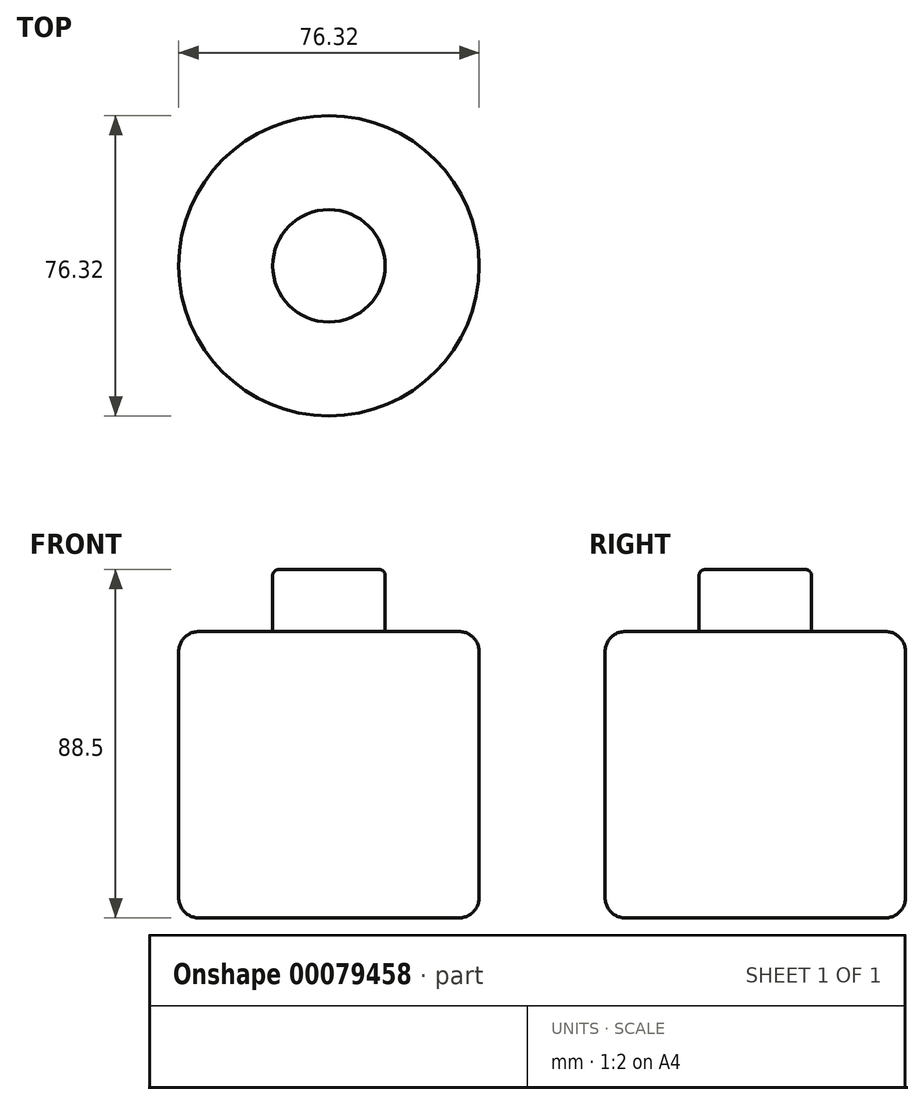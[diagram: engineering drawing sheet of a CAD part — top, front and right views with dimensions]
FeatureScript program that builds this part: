
annotation { "Feature Type Name" : "Feature", "Feature Type Description" : "" }
export const myFeature = defineFeature(function(context is Context, id is Id, definition is map)
    precondition{}
    {
        {
            var Q0;
            Q0=qCreatedBy(makeId("Top.planeOp"),FACE);
            var sketch = newSketch(context, id + "F0", { "sketchPlane" : qUnion([Q0])});
            skCircle(sketch, "E0", {"center": v(0, 0) * mm, "radius": 38.16 * mm});
            skSolve(sketch);
        }
        {
            var Q0;
            Q0=makeQuery(id+"F0.imprint","IMPRINT",FACE,{"disambiguationData":[TD([[makeQuery(id+"F0.imprint","IMPRINT",EDGE,{"derivedFrom":sQuery(id+"F0.wireOp",EDGE,"E0")}),1.0]])]});
            extrude(context, id + "F1", {"entities" : qUnion([Q0]), "depth" : 72.74 * mm});
        }
        {
            var Q0;
            Q0=makeQuery(id+"F1.opExtrude","CAP_EDGE",EDGE,{"disambiguationData":[OSD([sQuery(id+"F0.wireOp",EDGE,"E0")])],"isStart":false});
            var Q1;
            Q1=makeQuery(id+"F1.opExtrude","CAP_EDGE",EDGE,{"disambiguationData":[OSD([sQuery(id+"F0.wireOp",EDGE,"E0")])],"isStart":true});
            fillet(context, id + "F2", {"entities" : qUnion([Q0, Q1]), "radius" : 5.08 * mm, "tangentPropagation" : true, "allowEdgeOverflow" : false});
        }
        {
            var Q0;
            Q0=makeQuery(id+"F1.opExtrude","CAP_FACE",FACE,{"disambiguationData":[OSD([sQuery(id+"F0.wireOp",EDGE,"E0")])],"isStart":false});
            var sketch = newSketch(context, id + "F3", { "sketchPlane" : qUnion([Q0])});
            skCircle(sketch, "E1", {"center": v(0, 0) * mm, "radius": 14.3 * mm});
            skSolve(sketch);
        }
        {
            var Q0;
            Q0=makeQuery(id+"F3.imprint","IMPRINT",FACE,{"disambiguationData":[TD([[makeQuery(id+"F3.imprint","IMPRINT",EDGE,{"derivedFrom":sQuery(id+"F3.wireOp",EDGE,"E1")}),1.0]])]});
            extrude(context, id + "F4", {"entities" : qUnion([Q0]), "operationType" : NewBodyOperationType.ADD, "depth" : 15.75 * mm});
        }
        {
            var Q0;
            Q0=makeQuery(id+"F4.opExtrude","CAP_EDGE",EDGE,{"disambiguationData":[OSD([sQuery(id+"F3.wireOp",EDGE,"E1")])],"isStart":false});
            fillet(context, id + "F5", {"entities" : qUnion([Q0]), "radius" : 1.52 * mm, "tangentPropagation" : true, "allowEdgeOverflow" : false});
        }
    });
